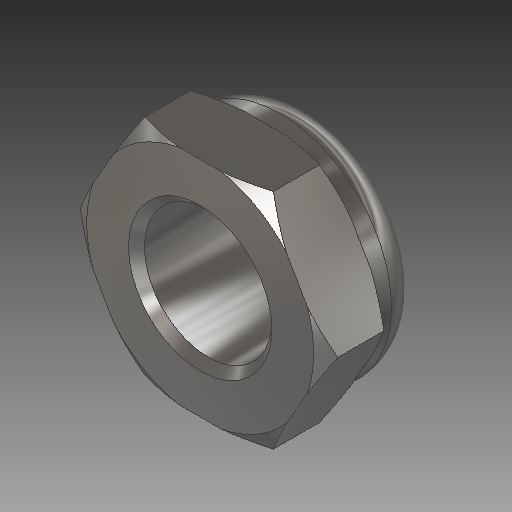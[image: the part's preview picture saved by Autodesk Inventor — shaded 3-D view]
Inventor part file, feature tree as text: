
AUTODESK INVENTOR PART (.ipt)
format: ipt  version: 2019.3 (Build 233278000, 278)  size: 231,936 bytes
history: native  units: mm
features: sketch x4, extrude x3, fillet x2, other x1, revolve x1, chamfer x1
ambient origin geometry x8: Origin, YZ Plane, XZ Plane, XY Plane, X Axis, Y Axis, Z Axis, Center Point
bodies: Body1 (feature_tree)
feature tree (12):
  other  "Твердое тело1"
  extrude  "Выдавливание1"  Depth=8.0mm
  revolve  "Вращение1"
  extrude  "Выдавливание2"  Depth=14.0mm
  fillet  "Сопряжение1"  Radius=4.0mm
  extrude  "Выдавливание3"  TaperAngle=60.0deg  [1 undecoded]
  fillet  "Сопряжение2"  Radius=1.0mm
  chamfer  "Фаска2"  Distance=3.5mm
  sketch  "Эскиз1"
  sketch  "Эскиз2"
  sketch  "Эскиз3"
  sketch  "Эскиз4"
note: 1 required parameter value undecoded (feature->parameter linkage not recoverable at this tier; creation-order binding heuristic only, values carry confidence <= 0.55)
